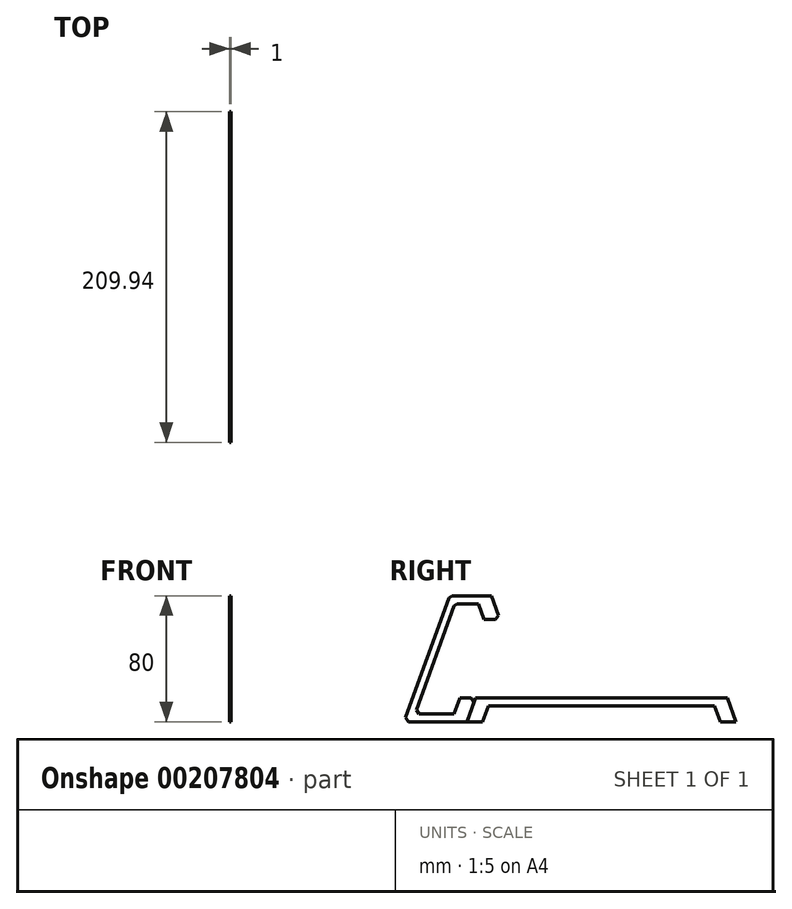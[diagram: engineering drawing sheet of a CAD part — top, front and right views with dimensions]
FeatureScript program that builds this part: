
annotation { "Feature Type Name" : "Feature", "Feature Type Description" : "" }
export const myFeature = defineFeature(function(context is Context, id is Id, definition is map)
    precondition{}
    {
        {
            var Q0;
            Q0=qCreatedBy(makeId("Right.planeOp"),FACE);
            var sketch = newSketch(context, id + "F0", { "sketchPlane" : qUnion([Q0])});
            skLineSegment(sketch, "E0", {"start": v(-59.09, -5.07) * mm, "end": v(-19.09, -5.07) * mm});
            skLineSegment(sketch, "E1", {"start": v(-19.09, -5.07) * mm, "end": v(-13.63, 9.93) * mm});
            skLineSegment(sketch, "E2", {"start": v(-13.63, 9.93) * mm, "end": v(-23.63, 9.93) * mm});
            skLineSegment(sketch, "E3", {"start": v(-23.63, 9.93) * mm, "end": v(-27.27, -0.07) * mm});
            skLineSegment(sketch, "E4", {"start": v(-27.27, -0.07) * mm, "end": v(-52.27, -0.07) * mm});
            skLineSegment(sketch, "E5", {"start": v(-52.27, -0.07) * mm, "end": v(-26.8, 69.93) * mm});
            skLineSegment(sketch, "E6", {"start": v(-26.8, 69.93) * mm, "end": v(-26.8, -0.07) * mm, "construction": true});
            skLineSegment(sketch, "E7", {"start": v(-19.09, -5.07) * mm, "end": v(-19.09, 9.93) * mm, "construction": true});
            skLineSegment(sketch, "E8", {"start": v(-59.09, -5.07) * mm, "end": v(-29.97, 74.93) * mm});
            skLineSegment(sketch, "E9", {"start": v(-29.97, 74.93) * mm, "end": v(-3.61, 74.93) * mm});
            skLineSegment(sketch, "E10", {"start": v(-26.8, 69.93) * mm, "end": v(-11.8, 69.93) * mm});
            skLineSegment(sketch, "E11", {"start": v(-11.8, 69.93) * mm, "end": v(-8.15, 59.93) * mm});
            skLineSegment(sketch, "E12", {"start": v(-8.15, 59.93) * mm, "end": v(-8.15, 69.93) * mm, "construction": true});
            skLineSegment(sketch, "E13", {"start": v(-8.15, 59.93) * mm, "end": v(1.85, 59.93) * mm});
            skLineSegment(sketch, "E14", {"start": v(1.85, 59.93) * mm, "end": v(-3.61, 74.93) * mm});
            skSolve(sketch);
        }
        {
            var Q0;
            Q0=makeQuery(id+"F0.imprint","IMPRINT",FACE,{"disambiguationData":[TD([[makeQuery(id+"F0.imprint","IMPRINT",EDGE,{"derivedFrom":sQuery(id+"F0.wireOp",EDGE,"E0")}),1.0]])]});
            extrude(context, id + "F1", {"entities" : qUnion([Q0]), "depth" : 1 * mm});
        }
        {
            var Q0;
            Q0=makeQuery(id+"F1.opExtrude","SWEPT_EDGE",EDGE,{"disambiguationData":[OSD([sQuery(id+"F0.wireOp",EDGE,"E0"),sQuery(id+"F0.wireOp",EDGE,"E8")])]});
            var Q1;
            Q1=makeQuery(id+"F1.opExtrude","SWEPT_EDGE",EDGE,{"disambiguationData":[OSD([sQuery(id+"F0.wireOp",EDGE,"E8"),sQuery(id+"F0.wireOp",EDGE,"E9")])]});
            var Q2;
            Q2=makeQuery(id+"F1.opExtrude","SWEPT_EDGE",EDGE,{"disambiguationData":[OSD([sQuery(id+"F0.wireOp",EDGE,"E5"),sQuery(id+"F0.wireOp",EDGE,"E10")])]});
            var Q3;
            Q3=makeQuery(id+"F1.opExtrude","SWEPT_EDGE",EDGE,{"disambiguationData":[OSD([sQuery(id+"F0.wireOp",EDGE,"E4"),sQuery(id+"F0.wireOp",EDGE,"E5")])]});
            var Q4;
            Q4=makeQuery(id+"F1.opExtrude","SWEPT_EDGE",EDGE,{"disambiguationData":[OSD([sQuery(id+"F0.wireOp",EDGE,"E1"),sQuery(id+"F0.wireOp",EDGE,"E2")])]});
            var Q5;
            Q5=makeQuery(id+"F1.opExtrude","SWEPT_EDGE",EDGE,{"disambiguationData":[OSD([sQuery(id+"F0.wireOp",EDGE,"E13"),sQuery(id+"F0.wireOp",EDGE,"E14")])]});
            chamfer(context, id + "F2", {"entities" : qUnion([Q0, Q1, Q2, Q3, Q4, Q5]), "width" : 2 * mm, "tangentPropagation" : true});
        }
        {
            var Q0;
            Q0=qCreatedBy(makeId("Right.planeOp"),FACE);
            var sketch = newSketch(context, id + "F3", { "sketchPlane" : qUnion([Q0])});
            skPoint(sketch, "E15.0", {"position": v(-19.09, -5.07) * mm});
            skLineSegment(sketch, "E16", {"start": v(-19.09, -5.07) * mm, "end": v(-9.09, -5.07) * mm});
            skLineSegment(sketch, "E17", {"start": v(-19.09, -5.07) * mm, "end": v(-13.63, 9.93) * mm});
            skLineSegment(sketch, "E18", {"start": v(-13.63, 9.93) * mm, "end": v(-13.63, -5.07) * mm, "construction": true});
            skLineSegment(sketch, "E19", {"start": v(-9.09, -5.07) * mm, "end": v(-5.45, 4.93) * mm});
            skLineSegment(sketch, "E20", {"start": v(-13.63, 9.93) * mm, "end": v(146.37, 9.93) * mm});
            skLineSegment(sketch, "E21", {"start": v(-5.45, 4.93) * mm, "end": v(138.2, 4.93) * mm});
            skLineSegment(sketch, "E22", {"start": v(-5.45, 4.93) * mm, "end": v(-5.45, 9.93) * mm, "construction": true});
            skLineSegment(sketch, "E23", {"start": v(138.2, 4.93) * mm, "end": v(141.83, -5.07) * mm});
            skLineSegment(sketch, "E24", {"start": v(141.83, -5.07) * mm, "end": v(151.83, -5.07) * mm});
            skLineSegment(sketch, "E25", {"start": v(151.83, -5.07) * mm, "end": v(146.37, 9.93) * mm});
            skLineSegment(sketch, "E26", {"start": v(141.83, 9.93) * mm, "end": v(141.83, -5.07) * mm, "construction": true});
            skSolve(sketch);
        }
        {
            var Q0;
            Q0=makeQuery(id+"F3.imprint","IMPRINT",FACE,{"disambiguationData":[TD([[makeQuery(id+"F3.imprint","IMPRINT",EDGE,{"derivedFrom":sQuery(id+"F3.wireOp",EDGE,"E16")}),1.0]])]});
            extrude(context, id + "F4", {"entities" : qUnion([Q0]), "depth" : 1 * mm});
        }
    });
